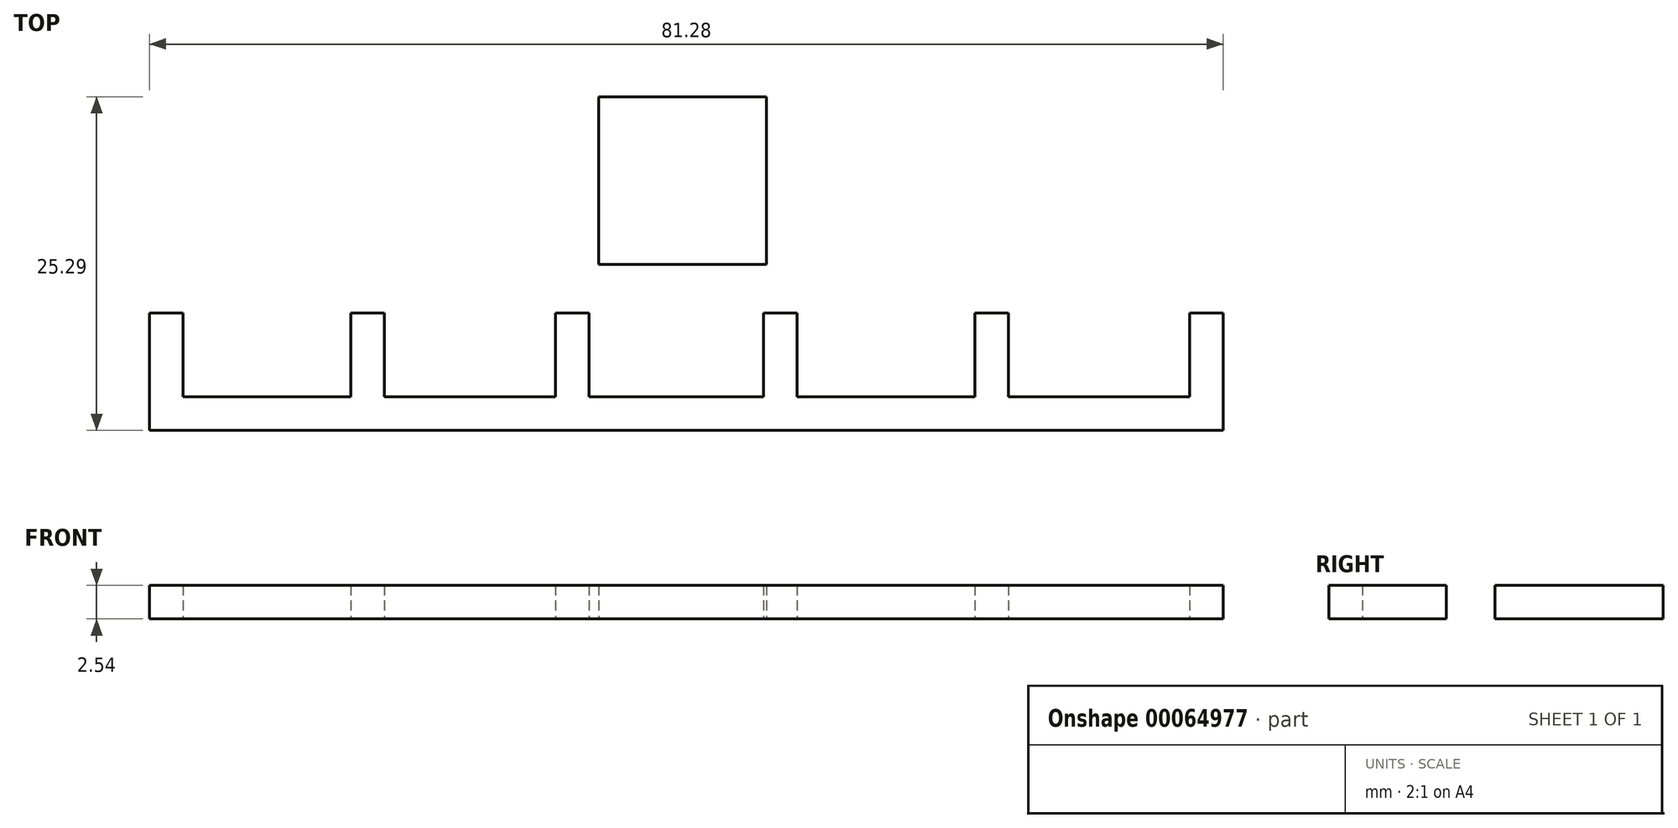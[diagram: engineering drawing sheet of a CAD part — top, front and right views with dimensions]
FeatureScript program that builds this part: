
annotation { "Feature Type Name" : "Feature", "Feature Type Description" : "" }
export const myFeature = defineFeature(function(context is Context, id is Id, definition is map)
    precondition{}
    {
        {
            var Q0;
            Q0=qCreatedBy(makeId("Top.planeOp"),FACE);
            var sketch = newSketch(context, id + "F0", { "sketchPlane" : qUnion([Q0])});
            skLineSegment(sketch, "E0.rect.bottom", {"start": v(6.35, 6.35) * mm, "end": v(-6.35, 6.35) * mm});
            skLineSegment(sketch, "E0.rect.top", {"start": v(6.35, -6.35) * mm, "end": v(-6.35, -6.35) * mm});
            skLineSegment(sketch, "E0.rect.left", {"start": v(6.35, 6.35) * mm, "end": v(6.35, -6.35) * mm});
            skLineSegment(sketch, "E0.rect.right", {"start": v(-6.35, 6.35) * mm, "end": v(-6.35, -6.35) * mm});
            skPoint(sketch, "E0.rect.middle", {"position": v(0, 0) * mm});
            skLineSegment(sketch, "E1.bottom", {"start": v(-37.82, -16.4) * mm, "end": v(-25.12, -16.4) * mm});
            skLineSegment(sketch, "E1.top", {"start": v(-40.36, -18.94) * mm, "end": v(40.92, -18.94) * mm});
            skLineSegment(sketch, "E2.top", {"start": v(-40.36, -10.05) * mm, "end": v(-37.82, -10.05) * mm});
            skLineSegment(sketch, "E2.right", {"start": v(-37.82, -16.4) * mm, "end": v(-37.82, -10.05) * mm});
            skLineSegment(sketch, "E3.top", {"start": v(-25.12, -10.05) * mm, "end": v(-22.58, -10.05) * mm});
            skLineSegment(sketch, "E3.left", {"start": v(-25.12, -16.4) * mm, "end": v(-25.12, -10.05) * mm});
            skLineSegment(sketch, "E3.right", {"start": v(-22.58, -16.4) * mm, "end": v(-22.58, -10.05) * mm});
            skLineSegment(sketch, "E4.top", {"start": v(40.92, -10.05) * mm, "end": v(38.38, -10.05) * mm});
            skLineSegment(sketch, "E4.right", {"start": v(38.38, -16.4) * mm, "end": v(38.38, -10.05) * mm});
            skLineSegment(sketch, "E5.top", {"start": v(-7.09, -10.05) * mm, "end": v(-9.63, -10.05) * mm});
            skLineSegment(sketch, "E5.left", {"start": v(-7.09, -16.4) * mm, "end": v(-7.09, -10.05) * mm});
            skLineSegment(sketch, "E5.right", {"start": v(-9.63, -16.4) * mm, "end": v(-9.63, -10.05) * mm});
            skLineSegment(sketch, "E6.top", {"start": v(6.12, -10.05) * mm, "end": v(8.66, -10.05) * mm});
            skLineSegment(sketch, "E6.left", {"start": v(6.12, -16.4) * mm, "end": v(6.12, -10.05) * mm});
            skLineSegment(sketch, "E6.right", {"start": v(8.66, -16.4) * mm, "end": v(8.66, -10.05) * mm});
            skLineSegment(sketch, "E7.top", {"start": v(22.12, -10.05) * mm, "end": v(24.66, -10.05) * mm});
            skLineSegment(sketch, "E7.left", {"start": v(22.12, -16.4) * mm, "end": v(22.12, -10.05) * mm});
            skLineSegment(sketch, "E7.right", {"start": v(24.66, -16.4) * mm, "end": v(24.66, -10.05) * mm});
            skLineSegment(sketch, "E8.trimOffspring", {"start": v(-22.58, -16.4) * mm, "end": v(-9.63, -16.4) * mm});
            skLineSegment(sketch, "E9.trimOffspring", {"start": v(-7.09, -16.4) * mm, "end": v(6.12, -16.4) * mm});
            skLineSegment(sketch, "E10.trimOffspring", {"start": v(8.66, -16.4) * mm, "end": v(22.12, -16.4) * mm});
            skLineSegment(sketch, "E11.trimOffspring", {"start": v(24.66, -16.4) * mm, "end": v(38.38, -16.4) * mm});
            skLineSegment(sketch, "E12", {"start": v(40.92, -10.05) * mm, "end": v(40.92, -18.94) * mm});
            skLineSegment(sketch, "E13", {"start": v(-40.36, -10.05) * mm, "end": v(-40.36, -18.94) * mm});
            skSolve(sketch);
        }
        {
            var Q0;
            Q0 = qSketchRegion(id + "F0", true);
            extrude(context, id + "F1", {"entities" : qUnion([Q0]), "depth" : 2.54 * mm});
        }
    });
